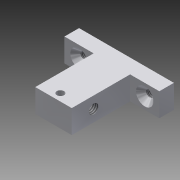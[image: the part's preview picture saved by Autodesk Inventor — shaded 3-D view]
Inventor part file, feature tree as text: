
AUTODESK INVENTOR PART (.ipt)
format: ipt  version: 2015 SP1 (Build 190203100, 203)  size: 150,016 bytes
history: native  units: in
note: dims shown in document units (in); Inventor stores cm internally (conversion verified against a paired STEP export)
features: extrude x3, hole x3, sketch x3, pattern_linear x1, projected_geometry x1
ambient origin geometry x8: Origin, YZ Plane, XZ Plane, XY Plane, X Axis, Y Axis, Z Axis, Center Point
bodies: Solid1 (feature_tree)
feature tree (11):
  extrude  "Extrusion1"  Depth=0.3937in TaperAngle=0.0deg
  hole  "Hole1"  [1 undecoded]
  hole  "Hole2"  [1 undecoded]
  extrude  "Extrusion4"  Depth=0.315in
  extrude  "Extrusion5"  Depth=0.7874in
  hole  "Hole3"  [1 undecoded]
  pattern_linear  "Rectangular Pattern1"  [2 undecoded]
  sketch  "Sketch1"  dims[d2=0.0in]
  sketch  "Sketch2"  dims[d3=0.0984in d4=0.2411in d5=0.0968in d6=0.2362in d7=0.1575in d8=0.0787in d9=90.0deg d10=0.315in d11=0.8108in]
  projected_geometry  "Projected Loop1"
  sketch  "Sketch4"  dims[d12=0.2953in d13=0.1575in d14=0.1276in d15=0.315in d16=0.1575in d17=0.0787in d18=90.0deg d19=0.4646in d20=0.8108in d26=0.3937in d27=0.0in d28=0.1969in d29=0.3937in d30=0.0in d31=0.1575in d32=0.1969in d33=0.0968in d34=0.2362in d35=0.2362in d36=0.0787in d37=90.0deg d38=0.315in d39=0.8108in d40=0.315in d41=0.7874in d43=0.8858in]
note: 5 required parameter values undecoded (feature->parameter linkage not recoverable at this tier; creation-order binding heuristic only, values carry confidence <= 0.55)
